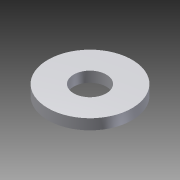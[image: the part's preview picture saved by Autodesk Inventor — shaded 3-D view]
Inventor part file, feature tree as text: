
AUTODESK INVENTOR PART (.ipt)
format: ipt  version: 2014 SP1 (Build 180222100, 222)  size: 90,112 bytes
history: native  units: in
note: dims shown in document units (in); Inventor stores cm internally (conversion verified against a paired STEP export)
features: other x1, imported_body x1, extrude x1, sketch x1
ambient origin geometry x8: Origin, YZ Plane, XZ Plane, XY Plane, X Axis, Y Axis, Z Axis, Center Point
bodies: Body1 (feature_tree)
feature tree (4):
  parser-record x1  (decoder bookkeeping rows leaked as tree rows — omitted from the tree; the rows remain in map.json)
  imported_body  "Base1"
  extrude  "Extrusion1"  [1 undecoded]
  sketch  "Sketch1"  dims[d0=0.0625in d1=0.0in]
note: 1 required parameter value undecoded (feature->parameter linkage not recoverable at this tier; creation-order binding heuristic only, values carry confidence <= 0.55)
